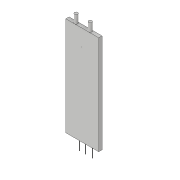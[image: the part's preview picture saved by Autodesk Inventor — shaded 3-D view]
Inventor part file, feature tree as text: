
AUTODESK INVENTOR PART (.ipt)
format: ipt  version: 2019 (Build 230136000, 136)  size: 96,256 bytes
history: native  units: in
note: dims shown in document units (in); Inventor stores cm internally (conversion verified against a paired STEP export)
features: sketch x4, extrude x3
ambient origin geometry x8: Origin, YZ Plane, XZ Plane, XY Plane, X Axis, Y Axis, Z Axis, Center Point
bodies: Solid1 (feature_tree)
feature tree (7):
  extrude  "Extrusion1"  Depth=1.1811in
  extrude  "Extrusion2"  Depth=0.0394in
  sketch  "Sketch3"  dims[d5=0.0984in d6=0.0in d7=0.1969in]
  extrude  "Extrusion3"  Depth=0.0984in
  sketch  "Sketch1"  dims[d0=0.3937in d1=1.1811in]
  sketch  "Sketch2"  dims[d2=0.0394in d3=0.0in d4=0.0394in]
  sketch  "Sketch4"  dims[d8=0.1969in d9=0.1969in d10=0.1969in d11=0.0039in d12=0.3937in d13=0.0in]
